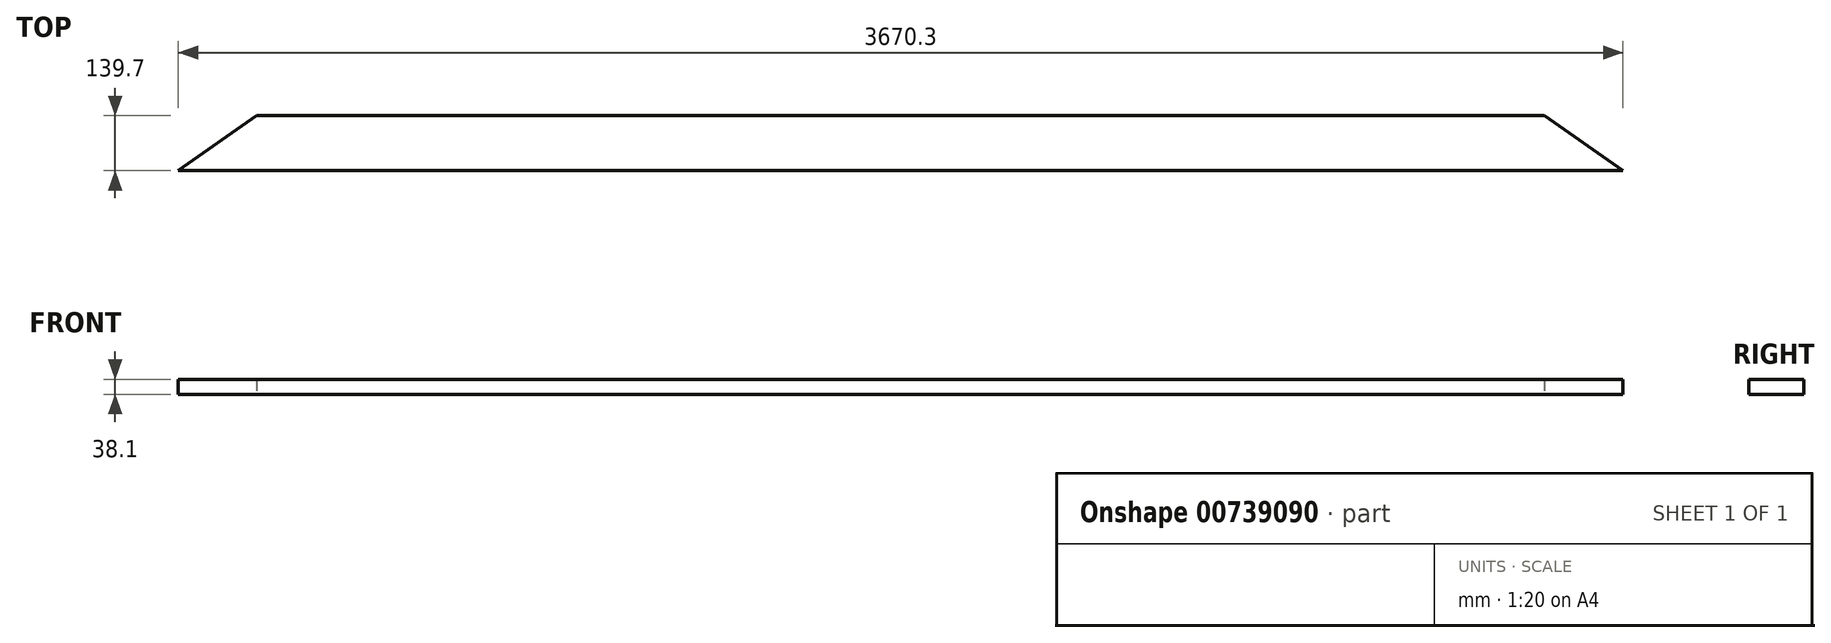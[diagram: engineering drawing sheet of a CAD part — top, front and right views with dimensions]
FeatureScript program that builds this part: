
annotation { "Feature Type Name" : "Feature", "Feature Type Description" : "" }
export const myFeature = defineFeature(function(context is Context, id is Id, definition is map)
    precondition{}
    {
        {
            var Q0;
            Q0=qCreatedBy(makeId("Top.planeOp"),FACE);
            var sketch = newSketch(context, id + "F0", { "sketchPlane" : qUnion([Q0])});
            skLineSegment(sketch, "E0", {"start": v(-1835.15, 0) * mm, "end": v(1835.15, 0) * mm});
            skLineSegment(sketch, "E1", {"start": v(0, 0) * mm, "end": v(0, 2090.5) * mm, "construction": true});
            skLineSegment(sketch, "E2", {"start": v(0, 1284.99) * mm, "end": v(-2084.55, -174.63) * mm});
            skLineSegment(sketch, "E3", {"start": v(-2084.55, -174.63) * mm, "end": v(-2084.55, -4.09) * mm});
            skLineSegment(sketch, "E4", {"start": v(-2084.55, -4.09) * mm, "end": v(0, 1455.53) * mm});
            skLineSegment(sketch, "E5.MirrorCS", {"start": v(2084.55, -4.09) * mm, "end": v(0, 1455.53) * mm});
            skLineSegment(sketch, "E6.MirrorCS", {"start": v(0, 1284.99) * mm, "end": v(2084.55, -174.63) * mm});
            skLineSegment(sketch, "E7.MirrorCS", {"start": v(2084.55, -174.63) * mm, "end": v(2084.55, -4.09) * mm});
            skLineSegment(sketch, "E8", {"start": v(-1635.64, 139.7) * mm, "end": v(1635.64, 139.7) * mm});
            skLineSegment(sketch, "E9", {"start": v(-2084.55, -174.63) * mm, "end": v(-2872.87, 951.22) * mm, "construction": true});
            skLineSegment(sketch, "E10", {"start": v(0, 1455.53) * mm, "end": v(-466, 2121.05) * mm, "construction": true});
            skPoint(sketch, "E11", {"position": v(0, 1045.25) * mm});
            skLineSegment(sketch, "E12", {"start": v(-2084.55, -4.09) * mm, "end": v(-2918.6, 1187.07) * mm, "construction": true});
            skLineSegment(sketch, "E13", {"start": v(-2084.55, -92.99) * mm, "end": v(-1967.95, -92.99) * mm});
            skLineSegment(sketch, "E14", {"start": v(-2084.55, -92.99) * mm, "end": v(-2122.65, -92.99) * mm});
            skLineSegment(sketch, "E15", {"start": v(-2122.65, -92.99) * mm, "end": v(-2122.65, -30.77) * mm});
            skLineSegment(sketch, "E16", {"start": v(-2122.65, -30.77) * mm, "end": v(-2084.55, -4.09) * mm});
            skLineSegment(sketch, "E17", {"start": v(2084.55, -4.09) * mm, "end": v(2103.6, -17.43) * mm});
            skLineSegment(sketch, "E18", {"start": v(2103.6, -17.43) * mm, "end": v(2103.6, -92.99) * mm});
            skLineSegment(sketch, "E19", {"start": v(2103.6, -92.99) * mm, "end": v(1967.95, -92.99) * mm});
            skSolve(sketch);
        }
        {
            var Q0;
            {var subQ0=sQuery(id+"F0.wireOp",EDGE,"E0");Q0=makeQuery(id+"F0.imprint","IMPRINT",FACE,{"disambiguationData":[TD([[makeQuery(id+"F0.imprint","IMPRINT",EDGE,{"derivedFrom":subQ0}),1.0]])]});}
            var Q1;
            {var subQ8=sQuery(id+"F0.wireOp",EDGE,"E4");Q1=makeQuery(id+"F0.imprint","IMPRINT",FACE,{"disambiguationData":[TD([[makeQuery(id+"F0.imprint","IMPRINT",EDGE,{"derivedFrom":subQ8}),-1.0]])]});}
            extrude(context, id + "F1", {"entities" : qUnion([Q0, Q1]), "depth" : 38.1 * mm, "offsetDistance" : 25.4 * mm});
        }
    });
